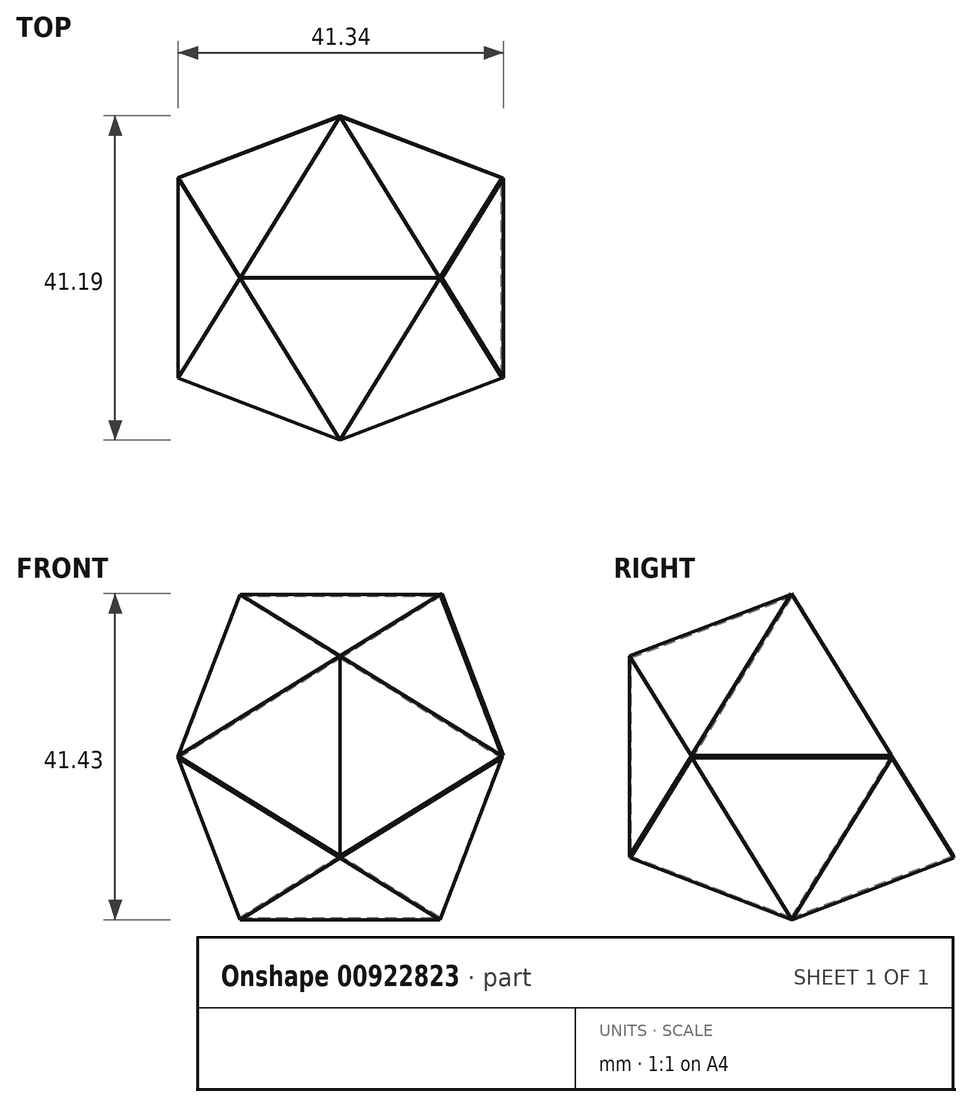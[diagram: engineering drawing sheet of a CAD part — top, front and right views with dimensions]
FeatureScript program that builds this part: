
annotation { "Feature Type Name" : "Feature", "Feature Type Description" : "" }
export const myFeature = defineFeature(function(context is Context, id is Id, definition is map)
    precondition{}
    {
        {
            var Q0;
            Q0=qCreatedBy(makeId("Front.planeOp"),FACE);
            var sketch = newSketch(context, id + "F0", { "sketchPlane" : qUnion([Q0])});
            skLineSegment(sketch, "E0.bottom", {"start": v(12.7, 20.55) * mm, "end": v(-12.7, 20.55) * mm});
            skLineSegment(sketch, "E0.top", {"start": v(12.7, -20.55) * mm, "end": v(-12.7, -20.55) * mm});
            skLineSegment(sketch, "E0.left", {"start": v(12.7, 20.55) * mm, "end": v(12.7, -20.55) * mm});
            skLineSegment(sketch, "E0.right", {"start": v(-12.7, 20.55) * mm, "end": v(-12.7, -20.55) * mm});
            skPoint(sketch, "E0.middle", {"position": v(0, 0) * mm});
            skSolve(sketch);
        }
        {
            var Q0;
            Q0=qCreatedBy(makeId("Right.planeOp"),FACE);
            var sketch = newSketch(context, id + "F1", { "sketchPlane" : qUnion([Q0])});
            skLineSegment(sketch, "E1.bottom", {"start": v(20.55, -12.7) * mm, "end": v(-20.55, -12.7) * mm});
            skLineSegment(sketch, "E1.top", {"start": v(20.55, 12.7) * mm, "end": v(-20.55, 12.7) * mm});
            skLineSegment(sketch, "E1.left", {"start": v(20.55, -12.7) * mm, "end": v(20.55, 12.7) * mm});
            skLineSegment(sketch, "E1.right", {"start": v(-20.55, -12.7) * mm, "end": v(-20.55, 12.7) * mm});
            skPoint(sketch, "E1.middle", {"position": v(0, 0) * mm});
            skSolve(sketch);
        }
        {
            var Q0;
            Q0=qCreatedBy(makeId("Top.planeOp"),FACE);
            var sketch = newSketch(context, id + "F2", { "sketchPlane" : qUnion([Q0])});
            skLineSegment(sketch, "E2.bottom", {"start": v(20.55, 12.7) * mm, "end": v(-20.55, 12.7) * mm});
            skLineSegment(sketch, "E2.top", {"start": v(20.55, -12.7) * mm, "end": v(-20.55, -12.7) * mm});
            skLineSegment(sketch, "E2.left", {"start": v(20.55, 12.7) * mm, "end": v(20.55, -12.7) * mm});
            skLineSegment(sketch, "E2.right", {"start": v(-20.55, 12.7) * mm, "end": v(-20.55, -12.7) * mm});
            skPoint(sketch, "E2.middle", {"position": v(0, 0) * mm});
            skSolve(sketch);
        }
        {
            var Q0;
            Q0=sQuery(id+"F0.wireOp",VERTEX,"E0.bottom.end");
            var Q1;
            Q1=sQuery(id+"F1.wireOp",VERTEX,"E1.top.end");
            var Q2;
            Q2=sQuery(id+"F2.wireOp",VERTEX,"E2.top.end");
            cPlane(context, id + "F3", {"entities" : qUnion([Q0, Q1, Q2]), "cplaneType" : CPlaneType.THREE_POINT, "offset" : 25.4 * mm, "width" : 152.4 * mm, "height" : 152.4 * mm});
        }
        {
            var Q0;
            Q0=qCreatedBy(id+"F3.planeOp",FACE);
            var sketch = newSketch(context, id + "F4", { "sketchPlane" : qUnion([Q0])});
            skLineSegment(sketch, "E3", {"start": v(-1.98, 14.53) * mm, "end": v(-11.6, -8.98) * mm});
            skLineSegment(sketch, "E4", {"start": v(-11.6, -8.98) * mm, "end": v(13.57, -5.55) * mm});
            skLineSegment(sketch, "E5", {"start": v(13.57, -5.55) * mm, "end": v(-1.98, 14.53) * mm});
            skSolve(sketch);
        }
        {
            var Q0;
            Q0=sQuery(id+"F1.wireOp",VERTEX,"E1.top.end");
            var Q1;
            Q1=sQuery(id+"F0.wireOp",VERTEX,"E0.bottom.end");
            var Q2;
            Q2=sQuery(id+"F0.wireOp",VERTEX,"E0.bottom.start");
            cPlane(context, id + "F5", {"entities" : qUnion([Q0, Q1, Q2]), "cplaneType" : CPlaneType.THREE_POINT, "offset" : 25.4 * mm, "width" : 152.4 * mm, "height" : 152.4 * mm});
        }
        {
            var Q0;
            Q0=qCreatedBy(id+"F5.planeOp",FACE);
            var sketch = newSketch(context, id + "F6", { "sketchPlane" : qUnion([Q0])});
            skLineSegment(sketch, "E6", {"start": v(-12.7, 7.33) * mm, "end": v(12.7, 7.33) * mm});
            skLineSegment(sketch, "E7", {"start": v(12.7, 7.33) * mm, "end": v(0, -14.68) * mm});
            skLineSegment(sketch, "E8", {"start": v(0, -14.68) * mm, "end": v(-12.7, 7.33) * mm});
            skSolve(sketch);
        }
        {
            var Q0;
            Q0=sQuery(id+"F1.wireOp",VERTEX,"E1.top.end");
            var Q1;
            Q1=sQuery(id+"F0.wireOp",VERTEX,"E0.bottom.start");
            var Q2;
            Q2=sQuery(id+"F2.wireOp",VERTEX,"E2.top.start");
            cPlane(context, id + "F7", {"entities" : qUnion([Q0, Q1, Q2]), "cplaneType" : CPlaneType.THREE_POINT, "offset" : 25.4 * mm, "width" : 152.4 * mm, "height" : 152.4 * mm});
        }
        {
            var Q0;
            Q0=qCreatedBy(id+"F7.planeOp",FACE);
            var sketch = newSketch(context, id + "F8", { "sketchPlane" : qUnion([Q0])});
            skLineSegment(sketch, "E9", {"start": v(1.98, 14.53) * mm, "end": v(11.6, -8.98) * mm});
            skLineSegment(sketch, "E10", {"start": v(11.6, -8.98) * mm, "end": v(-13.57, -5.55) * mm});
            skLineSegment(sketch, "E11", {"start": v(-13.57, -5.55) * mm, "end": v(1.98, 14.53) * mm});
            skSolve(sketch);
        }
        {
            var Q0;
            Q0=sQuery(id+"F1.wireOp",VERTEX,"E1.top.end");
            var Q1;
            Q1=sQuery(id+"F2.wireOp",VERTEX,"E2.top.start");
            var Q2;
            Q2=sQuery(id+"F1.wireOp",VERTEX,"E1.bottom.end");
            cPlane(context, id + "F9", {"entities" : qUnion([Q0, Q1, Q2]), "cplaneType" : CPlaneType.THREE_POINT, "offset" : 25.4 * mm, "width" : 152.4 * mm, "height" : 152.4 * mm});
        }
        {
            var Q0;
            Q0=qCreatedBy(id+"F9.planeOp",FACE);
            var sketch = newSketch(context, id + "F10", { "sketchPlane" : qUnion([Q0])});
            skLineSegment(sketch, "E12", {"start": v(-7.33, 12.7) * mm, "end": v(14.66, 0) * mm});
            skLineSegment(sketch, "E13", {"start": v(14.66, 0) * mm, "end": v(-7.33, -12.7) * mm});
            skLineSegment(sketch, "E14", {"start": v(-7.33, -12.7) * mm, "end": v(-7.33, 12.7) * mm});
            skSolve(sketch);
        }
        {
            var Q0;
            Q0=sQuery(id+"F1.wireOp",VERTEX,"E1.top.end");
            var Q1;
            Q1=sQuery(id+"F2.wireOp",VERTEX,"E2.top.end");
            var Q2;
            Q2=sQuery(id+"F1.wireOp",VERTEX,"E1.bottom.end");
            cPlane(context, id + "F11", {"entities" : qUnion([Q0, Q1, Q2]), "cplaneType" : CPlaneType.THREE_POINT, "offset" : 25.4 * mm, "width" : 152.4 * mm, "height" : 152.4 * mm});
        }
        {
            var Q0;
            Q0=qCreatedBy(id+"F11.planeOp",FACE);
            var sketch = newSketch(context, id + "F12", { "sketchPlane" : qUnion([Q0])});
            skLineSegment(sketch, "E15", {"start": v(-7.33, 12.7) * mm, "end": v(-7.33, -12.7) * mm});
            skLineSegment(sketch, "E16", {"start": v(-7.33, -12.7) * mm, "end": v(14.66, 0) * mm});
            skLineSegment(sketch, "E17", {"start": v(14.66, 0) * mm, "end": v(-7.33, 12.7) * mm});
            skSolve(sketch);
        }
        {
            var Q0;
            Q0=sQuery(id+"F1.wireOp",VERTEX,"E1.bottom.end");
            var Q1;
            Q1=sQuery(id+"F0.wireOp",VERTEX,"E0.top.start");
            var Q2;
            Q2=sQuery(id+"F2.wireOp",VERTEX,"E2.top.start");
            cPlane(context, id + "F13", {"entities" : qUnion([Q0, Q1, Q2]), "cplaneType" : CPlaneType.THREE_POINT, "offset" : 25.4 * mm, "width" : 152.4 * mm, "height" : 152.4 * mm});
        }
        {
            var Q0;
            Q0=qCreatedBy(id+"F13.planeOp",FACE);
            var sketch = newSketch(context, id + "F14", { "sketchPlane" : qUnion([Q0])});
            skLineSegment(sketch, "E18", {"start": v(-1.98, -14.53) * mm, "end": v(13.57, 5.55) * mm});
            skLineSegment(sketch, "E19", {"start": v(13.57, 5.55) * mm, "end": v(-11.6, 8.98) * mm});
            skLineSegment(sketch, "E20", {"start": v(-11.6, 8.98) * mm, "end": v(-1.98, -14.53) * mm});
            skSolve(sketch);
        }
        {
            var Q0;
            Q0=sQuery(id+"F1.wireOp",VERTEX,"E1.bottom.end");
            var Q1;
            Q1=sQuery(id+"F0.wireOp",VERTEX,"E0.top.end");
            var Q2;
            Q2=sQuery(id+"F2.wireOp",VERTEX,"E2.top.end");
            cPlane(context, id + "F15", {"entities" : qUnion([Q0, Q1, Q2]), "cplaneType" : CPlaneType.THREE_POINT, "offset" : 25.4 * mm, "width" : 152.4 * mm, "height" : 152.4 * mm});
        }
        {
            var Q0;
            Q0=qCreatedBy(id+"F15.planeOp",FACE);
            var sketch = newSketch(context, id + "F16", { "sketchPlane" : qUnion([Q0])});
            skLineSegment(sketch, "E21", {"start": v(-11.6, 8.98) * mm, "end": v(13.57, 5.55) * mm});
            skLineSegment(sketch, "E22", {"start": v(13.57, 5.55) * mm, "end": v(-1.98, -14.53) * mm});
            skLineSegment(sketch, "E23", {"start": v(-1.98, -14.53) * mm, "end": v(-11.6, 8.98) * mm});
            skSolve(sketch);
        }
        {
            var Q0;
            Q0=sQuery(id+"F0.wireOp",VERTEX,"E0.top.end");
            var Q1;
            Q1=sQuery(id+"F1.wireOp",VERTEX,"E1.bottom.start");
            var Q2;
            Q2=sQuery(id+"F0.wireOp",VERTEX,"E0.top.start");
            cPlane(context, id + "F17", {"entities" : qUnion([Q0, Q1, Q2]), "cplaneType" : CPlaneType.THREE_POINT, "offset" : 25.4 * mm, "width" : 152.4 * mm, "height" : 152.4 * mm});
        }
        {
            var Q0;
            Q0=qCreatedBy(id+"F17.planeOp",FACE);
            var sketch = newSketch(context, id + "F18", { "sketchPlane" : qUnion([Q0])});
            skLineSegment(sketch, "E24", {"start": v(-12.7, -7.33) * mm, "end": v(12.7, -7.33) * mm});
            skLineSegment(sketch, "E25", {"start": v(12.7, -7.33) * mm, "end": v(0, 14.66) * mm});
            skLineSegment(sketch, "E26", {"start": v(0, 14.66) * mm, "end": v(-12.7, -7.33) * mm});
            skSolve(sketch);
        }
        {
            var Q0;
            Q0=sQuery(id+"F0.wireOp",VERTEX,"E0.top.start");
            var Q1;
            Q1=sQuery(id+"F2.wireOp",VERTEX,"E2.bottom.start");
            var Q2;
            Q2=sQuery(id+"F2.wireOp",VERTEX,"E2.top.start");
            cPlane(context, id + "F19", {"entities" : qUnion([Q0, Q1, Q2]), "cplaneType" : CPlaneType.THREE_POINT, "offset" : 25.4 * mm, "width" : 152.4 * mm, "height" : 152.4 * mm});
        }
        {
            var Q0;
            Q0=qCreatedBy(id+"F19.planeOp",FACE);
            var sketch = newSketch(context, id + "F20", { "sketchPlane" : qUnion([Q0])});
            skLineSegment(sketch, "E27", {"start": v(0, -14.66) * mm, "end": v(-12.7, 7.33) * mm});
            skLineSegment(sketch, "E28", {"start": v(-12.7, 7.33) * mm, "end": v(12.7, 7.33) * mm});
            skLineSegment(sketch, "E29", {"start": v(12.7, 7.33) * mm, "end": v(0, -14.66) * mm});
            skSolve(sketch);
        }
        {
            var Q0;
            Q0=sQuery(id+"F2.wireOp",VERTEX,"E2.top.start");
            var Q1;
            Q1=sQuery(id+"F0.wireOp",VERTEX,"E0.bottom.start");
            var Q2;
            Q2=sQuery(id+"F2.wireOp",VERTEX,"E2.bottom.start");
            cPlane(context, id + "F21", {"entities" : qUnion([Q0, Q1, Q2]), "cplaneType" : CPlaneType.THREE_POINT, "offset" : 25.4 * mm, "width" : 152.4 * mm, "height" : 152.4 * mm});
        }
        {
            var Q0;
            Q0=qCreatedBy(id+"F21.planeOp",FACE);
            var sketch = newSketch(context, id + "F22", { "sketchPlane" : qUnion([Q0])});
            skLineSegment(sketch, "E30", {"start": v(-12.7, -7.33) * mm, "end": v(12.7, -7.33) * mm});
            skLineSegment(sketch, "E31", {"start": v(12.7, -7.33) * mm, "end": v(0, 14.66) * mm});
            skLineSegment(sketch, "E32", {"start": v(0, 14.66) * mm, "end": v(-12.7, -7.33) * mm});
            skSolve(sketch);
        }
        {
            var Q0;
            Q0=sQuery(id+"F0.wireOp",VERTEX,"E0.bottom.start");
            var Q1;
            Q1=sQuery(id+"F2.wireOp",VERTEX,"E2.bottom.start");
            var Q2;
            Q2=sQuery(id+"F1.wireOp",VERTEX,"E1.top.start");
            cPlane(context, id + "F23", {"entities" : qUnion([Q0, Q1, Q2]), "cplaneType" : CPlaneType.THREE_POINT, "offset" : 25.4 * mm, "width" : 152.4 * mm, "height" : 152.4 * mm});
        }
        {
            var Q0;
            Q0=sQuery(id+"F1.wireOp",VERTEX,"E1.top.start");
            var Q1;
            Q1=sQuery(id+"F0.wireOp",VERTEX,"E0.bottom.end");
            var Q2;
            Q2=sQuery(id+"F0.wireOp",VERTEX,"E0.bottom.start");
            cPlane(context, id + "F24", {"entities" : qUnion([Q0, Q1, Q2]), "cplaneType" : CPlaneType.THREE_POINT, "offset" : 25.4 * mm, "width" : 152.4 * mm, "height" : 152.4 * mm});
        }
        {
            var Q0;
            Q0=sQuery(id+"F1.wireOp",VERTEX,"E1.top.start");
            var Q1;
            Q1=sQuery(id+"F2.wireOp",VERTEX,"E2.bottom.end");
            var Q2;
            Q2=sQuery(id+"F0.wireOp",VERTEX,"E0.bottom.end");
            cPlane(context, id + "F25", {"entities" : qUnion([Q0, Q1, Q2]), "cplaneType" : CPlaneType.THREE_POINT, "offset" : 25.4 * mm, "width" : 152.4 * mm, "height" : 152.4 * mm});
        }
        {
            var Q0;
            Q0=sQuery(id+"F1.wireOp",VERTEX,"E1.bottom.start");
            var Q1;
            Q1=sQuery(id+"F1.wireOp",VERTEX,"E1.top.start");
            var Q2;
            Q2=sQuery(id+"F2.wireOp",VERTEX,"E2.bottom.end");
            cPlane(context, id + "F26", {"entities" : qUnion([Q0, Q1, Q2]), "cplaneType" : CPlaneType.THREE_POINT, "offset" : 25.4 * mm, "width" : 152.4 * mm, "height" : 152.4 * mm});
        }
        {
            var Q0;
            Q0=sQuery(id+"F1.wireOp",VERTEX,"E1.bottom.start");
            var Q1;
            Q1=sQuery(id+"F2.wireOp",VERTEX,"E2.bottom.start");
            var Q2;
            Q2=sQuery(id+"F1.wireOp",VERTEX,"E1.top.start");
            cPlane(context, id + "F27", {"entities" : qUnion([Q0, Q1, Q2]), "cplaneType" : CPlaneType.THREE_POINT, "offset" : 25.4 * mm, "width" : 152.4 * mm, "height" : 152.4 * mm});
        }
        {
            var Q0;
            Q0=sQuery(id+"F0.wireOp",VERTEX,"E0.top.end");
            var Q1;
            Q1=sQuery(id+"F2.wireOp",VERTEX,"E2.bottom.end");
            var Q2;
            Q2=sQuery(id+"F1.wireOp",VERTEX,"E1.bottom.start");
            cPlane(context, id + "F28", {"entities" : qUnion([Q0, Q1, Q2]), "cplaneType" : CPlaneType.THREE_POINT, "offset" : 25.4 * mm, "width" : 152.4 * mm, "height" : 152.4 * mm});
        }
        {
            var Q0;
            Q0=qCreatedBy(id+"F28.planeOp",FACE);
            var sketch = newSketch(context, id + "F29", { "sketchPlane" : qUnion([Q0])});
            skLineSegment(sketch, "E33", {"start": v(-1.98, -14.53) * mm, "end": v(-11.6, 8.98) * mm});
            skLineSegment(sketch, "E34", {"start": v(-11.6, 8.98) * mm, "end": v(13.57, 5.55) * mm});
            skLineSegment(sketch, "E35", {"start": v(13.57, 5.55) * mm, "end": v(-1.98, -14.53) * mm});
            skSolve(sketch);
        }
        {
            var Q0;
            Q0=sQuery(id+"F2.wireOp",VERTEX,"E2.bottom.end");
            var Q1;
            Q1=sQuery(id+"F0.wireOp",VERTEX,"E0.top.end");
            var Q2;
            Q2=sQuery(id+"F2.wireOp",VERTEX,"E2.top.end");
            cPlane(context, id + "F30", {"entities" : qUnion([Q0, Q1, Q2]), "cplaneType" : CPlaneType.THREE_POINT, "offset" : 25.4 * mm, "width" : 152.4 * mm, "height" : 152.4 * mm});
        }
        {
            var Q0;
            Q0=qCreatedBy(id+"F30.planeOp",FACE);
            var sketch = newSketch(context, id + "F31", { "sketchPlane" : qUnion([Q0])});
            skLineSegment(sketch, "E36", {"start": v(0, -14.66) * mm, "end": v(-12.7, 7.33) * mm});
            skLineSegment(sketch, "E37", {"start": v(-12.7, 7.33) * mm, "end": v(12.7, 7.33) * mm});
            skLineSegment(sketch, "E38", {"start": v(12.7, 7.33) * mm, "end": v(0, -14.66) * mm});
            skSolve(sketch);
        }
        {
            var Q0;
            Q0=sQuery(id+"F2.wireOp",VERTEX,"E2.bottom.end");
            var Q1;
            Q1=sQuery(id+"F2.wireOp",VERTEX,"E2.top.end");
            var Q2;
            Q2=sQuery(id+"F0.wireOp",VERTEX,"E0.bottom.end");
            cPlane(context, id + "F32", {"entities" : qUnion([Q0, Q1, Q2]), "cplaneType" : CPlaneType.THREE_POINT, "offset" : 25.4 * mm, "width" : 152.4 * mm, "height" : 152.4 * mm});
        }
        {
            var Q0;
            Q0=qCreatedBy(id+"F32.planeOp",FACE);
            var sketch = newSketch(context, id + "F33", { "sketchPlane" : qUnion([Q0])});
            skLineSegment(sketch, "E39", {"start": v(-12.7, -7.33) * mm, "end": v(12.7, -7.33) * mm});
            skLineSegment(sketch, "E40", {"start": v(12.7, -7.33) * mm, "end": v(0, 14.66) * mm});
            skLineSegment(sketch, "E41", {"start": v(0, 14.66) * mm, "end": v(-12.7, -7.33) * mm});
            skSolve(sketch);
        }
        {
            var Q0;
            Q0=sQuery(id+"F10.wireOp",VERTEX,"E13.end");
            var Q1;
            Q1=sQuery(id+"F16.wireOp",VERTEX,"E22.end");
            var Q2;
            Q2=sQuery(id+"F14.wireOp",VERTEX,"E18.start");
            cPlane(context, id + "F34", {"entities" : qUnion([Q0, Q1, Q2]), "cplaneType" : CPlaneType.THREE_POINT, "offset" : 25.4 * mm, "width" : 152.4 * mm, "height" : 152.4 * mm});
        }
        {
            var Q0;
            Q0=qCreatedBy(id+"F34.planeOp",FACE);
            var sketch = newSketch(context, id + "F35", { "sketchPlane" : qUnion([Q0])});
            skLineSegment(sketch, "E42", {"start": v(0, -14.66) * mm, "end": v(-12.7, 7.33) * mm});
            skLineSegment(sketch, "E43", {"start": v(-12.7, 7.33) * mm, "end": v(12.7, 7.33) * mm});
            skLineSegment(sketch, "E44", {"start": v(12.7, 7.33) * mm, "end": v(0, -14.66) * mm});
            skSolve(sketch);
        }
        {
            var Q0;
            Q0=sQuery(id+"F14.wireOp",VERTEX,"E18.start");
            var Q1;
            Q1=sQuery(id+"F18.wireOp",VERTEX,"E25.end");
            var Q2;
            Q2=sQuery(id+"F20.wireOp",VERTEX,"E27.end");
            cPlane(context, id + "F36", {"entities" : qUnion([Q0, Q1, Q2]), "cplaneType" : CPlaneType.THREE_POINT, "offset" : 25.4 * mm, "width" : 152.4 * mm, "height" : 152.4 * mm});
        }
        {
            var Q0;
            Q0=qCreatedBy(id+"F36.planeOp",FACE);
            var sketch = newSketch(context, id + "F37", { "sketchPlane" : qUnion([Q0])});
            skLineSegment(sketch, "E45", {"start": v(-13.57, 5.55) * mm, "end": v(1.98, -14.53) * mm});
            skLineSegment(sketch, "E46", {"start": v(1.98, -14.53) * mm, "end": v(11.6, 8.98) * mm});
            skLineSegment(sketch, "E47", {"start": v(11.6, 8.98) * mm, "end": v(-13.57, 5.55) * mm});
            skSolve(sketch);
        }
        {
            var Q0;
            Q0=makeQuery(id+"F18.imprint","IMPRINT",FACE,{"disambiguationData":[TD([[makeQuery(id+"F18.imprint","IMPRINT",EDGE,{"derivedFrom":sQuery(id+"F18.wireOp",EDGE,"E24")}),1.0]])]});
            var Q1;
            Q1=makeQuery(id+"F29.imprint","IMPRINT",FACE,{"disambiguationData":[TD([[makeQuery(id+"F29.imprint","IMPRINT",EDGE,{"derivedFrom":sQuery(id+"F29.wireOp",EDGE,"E33")}),-1.0]])]});
            var Q2;
            Q2=makeQuery(id+"F37.imprint","IMPRINT",FACE,{"disambiguationData":[TD([[makeQuery(id+"F37.imprint","IMPRINT",EDGE,{"derivedFrom":sQuery(id+"F37.wireOp",EDGE,"E45")}),1.0]])]});
            var Q3;
            Q3=makeQuery(id+"F20.imprint","IMPRINT",FACE,{"disambiguationData":[TD([[makeQuery(id+"F20.imprint","IMPRINT",EDGE,{"derivedFrom":sQuery(id+"F20.wireOp",EDGE,"E27")}),-1.0]])]});
            var Q4;
            Q4=makeQuery(id+"F22.imprint","IMPRINT",FACE,{"disambiguationData":[TD([[makeQuery(id+"F22.imprint","IMPRINT",EDGE,{"derivedFrom":sQuery(id+"F22.wireOp",EDGE,"E30")}),1.0]])]});
            var Q5;
            Q5=makeQuery(id+"F14.imprint","IMPRINT",FACE,{"disambiguationData":[TD([[makeQuery(id+"F14.imprint","IMPRINT",EDGE,{"derivedFrom":sQuery(id+"F14.wireOp",EDGE,"E18")}),1.0]])]});
            var Q6;
            Q6=makeQuery(id+"F10.imprint","IMPRINT",FACE,{"disambiguationData":[TD([[makeQuery(id+"F10.imprint","IMPRINT",EDGE,{"derivedFrom":sQuery(id+"F10.wireOp",EDGE,"E12")}),-1.0]])]});
            var Q7;
            Q7=makeQuery(id+"F35.imprint","IMPRINT",FACE,{"disambiguationData":[TD([[makeQuery(id+"F35.imprint","IMPRINT",EDGE,{"derivedFrom":sQuery(id+"F35.wireOp",EDGE,"E42")}),-1.0]])]});
            var Q8;
            Q8=makeQuery(id+"F12.imprint","IMPRINT",FACE,{"disambiguationData":[TD([[makeQuery(id+"F12.imprint","IMPRINT",EDGE,{"derivedFrom":sQuery(id+"F12.wireOp",EDGE,"E15")}),1.0]])]});
            var Q9;
            Q9=makeQuery(id+"F16.imprint","IMPRINT",FACE,{"disambiguationData":[TD([[makeQuery(id+"F16.imprint","IMPRINT",EDGE,{"derivedFrom":sQuery(id+"F16.wireOp",EDGE,"E21")}),-1.0]])]});
            var Q10;
            Q10=makeQuery(id+"F8.imprint","IMPRINT",FACE,{"disambiguationData":[TD([[makeQuery(id+"F8.imprint","IMPRINT",EDGE,{"derivedFrom":sQuery(id+"F8.wireOp",EDGE,"E9")}),-1.0]])]});
            var Q11;
            Q11=makeQuery(id+"F6.imprint","IMPRINT",FACE,{"disambiguationData":[TD([[makeQuery(id+"F6.imprint","IMPRINT",EDGE,{"derivedFrom":sQuery(id+"F6.wireOp",EDGE,"E6")}),-1.0]])]});
            var Q12;
            Q12=makeQuery(id+"F4.imprint","IMPRINT",FACE,{"disambiguationData":[TD([[makeQuery(id+"F4.imprint","IMPRINT",EDGE,{"derivedFrom":sQuery(id+"F4.wireOp",EDGE,"E3")}),1.0]])]});
            var Q13;
            Q13=makeQuery(id+"F33.imprint","IMPRINT",FACE,{"disambiguationData":[TD([[makeQuery(id+"F33.imprint","IMPRINT",EDGE,{"derivedFrom":sQuery(id+"F33.wireOp",EDGE,"E39")}),1.0]])]});
            var Q14;
            Q14=makeQuery(id+"F31.imprint","IMPRINT",FACE,{"disambiguationData":[TD([[makeQuery(id+"F31.imprint","IMPRINT",EDGE,{"derivedFrom":sQuery(id+"F31.wireOp",EDGE,"E36")}),-1.0]])]});
            extrude(context, id + "F38", {"entities" : qUnion([Q0, Q1, Q2, Q3, Q4, Q5, Q6, Q7, Q8, Q9, Q10, Q11, Q12, Q13, Q14]), "oppositeDirection" : true, "depth" : 0.25 * mm, "offsetDistance" : 25.4 * mm});
        }
        {
            var Q0;
            Q0=makeQuery(id+"F38.opExtrude","CAP_FACE",FACE,{"disambiguationData":[OSD([sQuery(id+"F22.wireOp",EDGE,"E30"),sQuery(id+"F22.wireOp",EDGE,"E31"),sQuery(id+"F22.wireOp",EDGE,"E32")]),OD(1.0)],"isStart":false});
            extrude(context, id + "F39", {"entities" : qUnion([Q0]), "operationType" : NewBodyOperationType.ADD, "depth" : 0.25 * mm, "offsetDistance" : 25.4 * mm});
        }
    });
